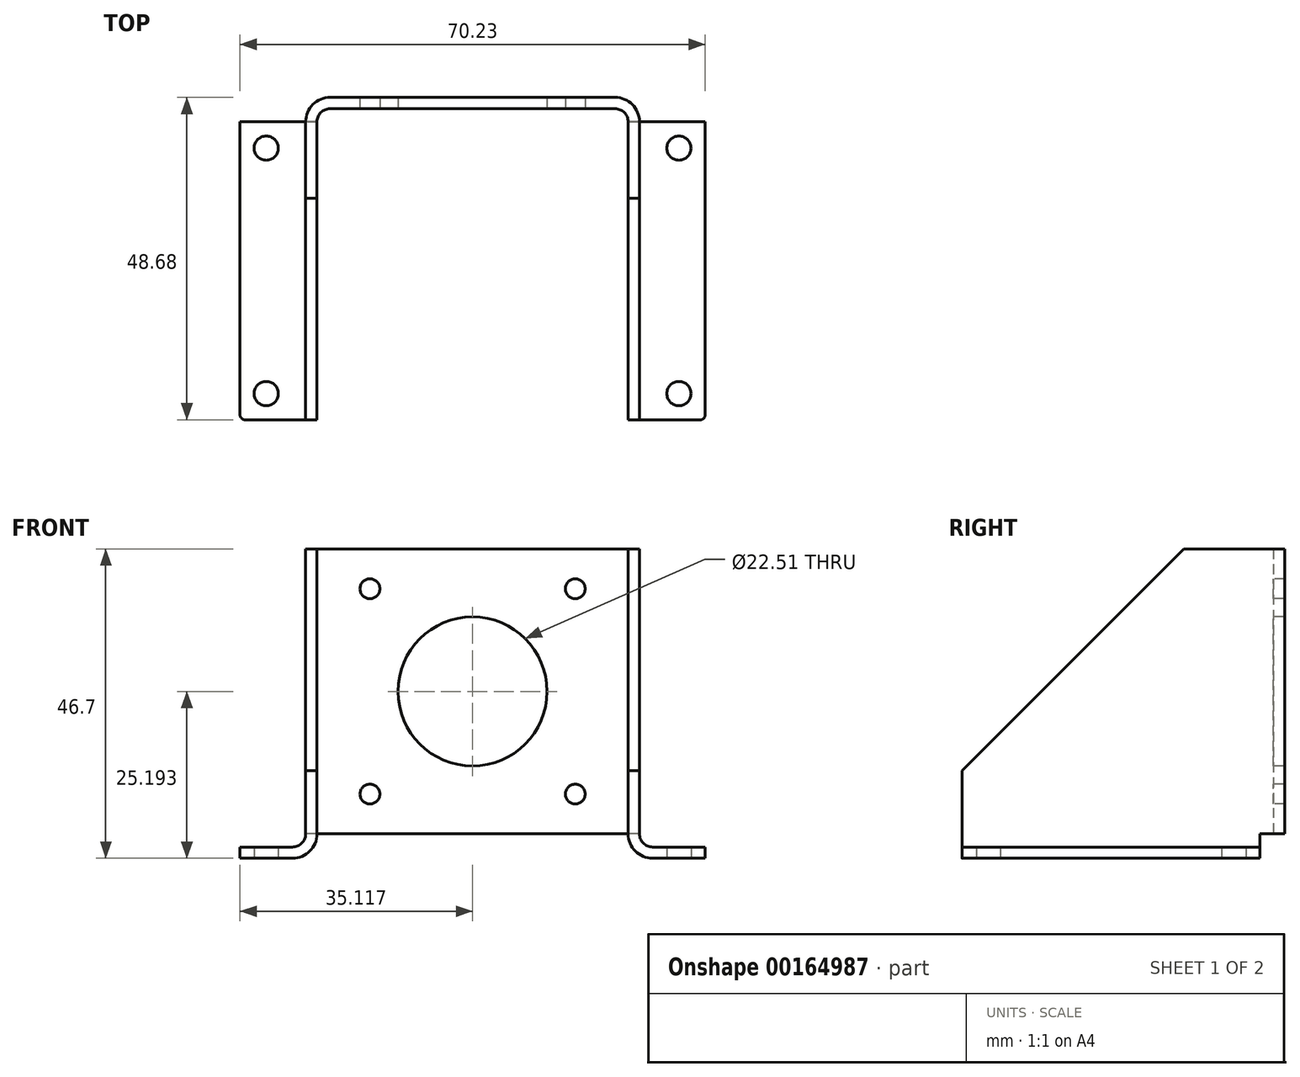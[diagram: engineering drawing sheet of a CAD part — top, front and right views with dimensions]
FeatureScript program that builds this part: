
annotation { "Feature Type Name" : "Feature", "Feature Type Description" : "" }
export const myFeature = defineFeature(function(context is Context, id is Id, definition is map)
    precondition{}
    {
        {
            var Q0;
            Q0=qCreatedBy(makeId("Top.planeOp"),FACE);
            var sketch = newSketch(context, id + "F0", { "sketchPlane" : qUnion([Q0])});
            skLineSegment(sketch, "E0.bottom", {"start": v(0, 0) * mm, "end": v(-1.7, 0) * mm});
            skLineSegment(sketch, "E1.left", {"start": v(0, 0) * mm, "end": v(0, 46.97) * mm});
            skLineSegment(sketch, "E1.right", {"start": v(-1.7, 0) * mm, "end": v(-1.7, 48.68) * mm});
            skLineSegment(sketch, "E2.bottom", {"start": v(0, 46.97) * mm, "end": v(46.97, 46.97) * mm});
            skLineSegment(sketch, "E2.top", {"start": v(-1.7, 48.68) * mm, "end": v(48.68, 48.68) * mm});
            skLineSegment(sketch, "E3.top", {"start": v(46.97, 0) * mm, "end": v(48.68, 0) * mm});
            skLineSegment(sketch, "E3.left", {"start": v(46.97, 46.97) * mm, "end": v(46.97, 0) * mm});
            skLineSegment(sketch, "E3.right", {"start": v(48.68, 48.68) * mm, "end": v(48.68, 0) * mm});
            skLineSegment(sketch, "E4", {"start": v(0, 46.97) * mm, "end": v(-1.7, 46.97) * mm, "construction": true});
            skLineSegment(sketch, "E5", {"start": v(0, 46.97) * mm, "end": v(0, 48.68) * mm, "construction": true});
            skLineSegment(sketch, "E6", {"start": v(46.97, 46.97) * mm, "end": v(48.68, 46.97) * mm, "construction": true});
            skLineSegment(sketch, "E7", {"start": v(46.97, 46.97) * mm, "end": v(46.97, 48.68) * mm, "construction": true});
            skSolve(sketch);
        }
        {
            var Q0;
            Q0=qSketchRegion(id+"F0",true);
            extrude(context, id + "F1", {"entities" : qUnion([Q0]), "depth" : 43 * mm});
        }
        {
            var Q0;
            Q0=makeQuery(id+"F1.opExtrude","SWEPT_FACE",FACE,{"disambiguationData":[OSD([sQuery(id+"F0.wireOp",EDGE,"E2.bottom")])]});
            cPlane(context, id + "F2", {"entities" : qUnion([Q0]), "cplaneType" : CPlaneType.OFFSET, "offset" : 1.98 * mm, "width" : 152.4 * mm, "height" : 152.4 * mm});
        }
        {
            var Q0;
            Q0=makeQuery(id+"F1.opExtrude","SWEPT_FACE",FACE,{"disambiguationData":[OSD([sQuery(id+"F0.wireOp",EDGE,"E3.top")])]});
            var sketch = newSketch(context, id + "F3", { "sketchPlane" : qUnion([Q0])});
            skLineSegment(sketch, "E8.bottom", {"start": v(46.97, 0) * mm, "end": v(48.68, 0) * mm});
            skLineSegment(sketch, "E8.left", {"start": v(46.97, 0) * mm, "end": v(46.97, -3.7) * mm});
            skLineSegment(sketch, "E8.right", {"start": v(48.68, 0) * mm, "end": v(48.68, -1.98) * mm});
            skLineSegment(sketch, "E9.bottom", {"start": v(48.68, -1.98) * mm, "end": v(58.6, -1.98) * mm});
            skLineSegment(sketch, "E9.top", {"start": v(46.97, -3.7) * mm, "end": v(58.6, -3.7) * mm});
            skLineSegment(sketch, "E9.right", {"start": v(58.6, -1.98) * mm, "end": v(58.6, -3.7) * mm});
            skLineSegment(sketch, "E10.bottom", {"start": v(-1.7, 0) * mm, "end": v(0, 0) * mm});
            skLineSegment(sketch, "E10.left", {"start": v(-1.7, 0) * mm, "end": v(-1.7, -1.98) * mm});
            skLineSegment(sketch, "E10.right", {"start": v(0, 0) * mm, "end": v(0, -3.7) * mm});
            skLineSegment(sketch, "E11.bottom", {"start": v(-1.7, -1.98) * mm, "end": v(-11.63, -1.98) * mm});
            skLineSegment(sketch, "E11.top", {"start": v(0, -3.7) * mm, "end": v(-11.63, -3.7) * mm});
            skLineSegment(sketch, "E11.right", {"start": v(-11.63, -1.98) * mm, "end": v(-11.63, -3.7) * mm});
            skSolve(sketch);
        }
        {
            var Q0;
            Q0=makeQuery(id+"F3.imprint","IMPRINT",FACE,{"disambiguationData":[TD([[makeQuery(id+"F3.imprint","IMPRINT",EDGE,{"derivedFrom":sQuery(id+"F3.wireOp",EDGE,"E8.bottom")}),-1.0]])]});
            var Q1;
            Q1=makeQuery(id+"F3.imprint","IMPRINT",FACE,{"disambiguationData":[TD([[makeQuery(id+"F3.imprint","IMPRINT",EDGE,{"derivedFrom":sQuery(id+"F3.wireOp",EDGE,"E10.bottom")}),-1.0]])]});
            var Q2;
            Q2=qCreatedBy(id+"F2.planeOp",FACE);
            extrude(context, id + "F4", {"entities" : qUnion([Q0, Q1]), "operationType" : NewBodyOperationType.ADD, "endBound" : BoundingType.UP_TO_SURFACE, "oppositeDirection" : true, "endBoundEntityFace" : qUnion([Q2]), "depth" : 25.4 * mm});
        }
        {
            var Q0;
            Q0=makeQuery(id+"F1.opExtrude","SWEPT_EDGE",EDGE,{"disambiguationData":[OSD([sQuery(id+"F0.wireOp",EDGE,"E1.left"),sQuery(id+"F0.wireOp",EDGE,"E2.bottom")])]});
            var Q1;
            Q1=makeQuery(id+"F1.opExtrude","SWEPT_EDGE",EDGE,{"disambiguationData":[OSD([sQuery(id+"F0.wireOp",EDGE,"E2.bottom"),sQuery(id+"F0.wireOp",EDGE,"E3.left")])]});
            var Q2;
            Q2=makeQuery(id+"F4.opExtrude","SWEPT_EDGE",EDGE,{"disambiguationData":[OSD([sQuery(id+"F3.wireOp",EDGE,"E10.left"),sQuery(id+"F3.wireOp",EDGE,"E11.bottom")])]});
            var Q3;
            Q3=makeQuery(id+"F4.opExtrude","SWEPT_EDGE",EDGE,{"disambiguationData":[OSD([sQuery(id+"F3.wireOp",EDGE,"E8.right"),sQuery(id+"F3.wireOp",EDGE,"E9.bottom")])]});
            fillet(context, id + "F5", {"entities" : qUnion([Q0, Q1, Q2, Q3]), "radius" : 1.98 * mm, "tangentPropagation" : true, "allowEdgeOverflow" : false});
        }
        {
            var Q0;
            Q0=makeQuery(id+"F1.opExtrude","SWEPT_EDGE",EDGE,{"disambiguationData":[OSD([sQuery(id+"F0.wireOp",EDGE,"E2.top"),sQuery(id+"F0.wireOp",EDGE,"E3.right")])]});
            var Q1;
            Q1=makeQuery(id+"F1.opExtrude","SWEPT_EDGE",EDGE,{"disambiguationData":[OSD([sQuery(id+"F0.wireOp",EDGE,"E1.right"),sQuery(id+"F0.wireOp",EDGE,"E2.top")])]});
            var Q2;
            Q2=makeQuery(id+"F4.opExtrude","SWEPT_EDGE",EDGE,{"disambiguationData":[OSD([sQuery(id+"F3.wireOp",EDGE,"E10.right"),sQuery(id+"F3.wireOp",EDGE,"E11.top")])]});
            var Q3;
            Q3=makeQuery(id+"F4.opExtrude","SWEPT_EDGE",EDGE,{"disambiguationData":[OSD([sQuery(id+"F3.wireOp",EDGE,"E8.left"),sQuery(id+"F3.wireOp",EDGE,"E9.top")])]});
            fillet(context, id + "F6", {"entities" : qUnion([Q0, Q1, Q2, Q3]), "radius" : 3.7 * mm, "tangentPropagation" : true, "allowEdgeOverflow" : false});
        }
        {
            var Q0;
            Q0=makeQuery(id+"F1.opExtrude","CAP_EDGE",EDGE,{"disambiguationData":[OSD([sQuery(id+"F0.wireOp",EDGE,"E0.bottom")])],"isStart":false});
            var Q1;
            Q1=makeQuery(id+"F1.opExtrude","CAP_EDGE",EDGE,{"disambiguationData":[OSD([sQuery(id+"F0.wireOp",EDGE,"E3.top")])],"isStart":false});
            chamfer(context, id + "F7", {"entities" : qUnion([Q0, Q1]), "width" : 33.48 * mm, "tangentPropagation" : true});
        }
        {
            var Q0;
            Q0=makeQuery(id+"F1.opExtrude","SWEPT_FACE",FACE,{"disambiguationData":[OSD([sQuery(id+"F0.wireOp",EDGE,"E2.bottom")])]});
            var sketch = newSketch(context, id + "F8", { "sketchPlane" : qUnion([Q0])});
            skLineSegment(sketch, "E12", {"start": v(23.49, 43) * mm, "end": v(23.49, 0) * mm, "construction": true});
            skLineSegment(sketch, "E13.bottom", {"start": v(38.99, 37) * mm, "end": v(7.99, 37) * mm, "construction": true});
            skLineSegment(sketch, "E13.top", {"start": v(38.99, 6) * mm, "end": v(7.99, 6) * mm, "construction": true});
            skLineSegment(sketch, "E13.left", {"start": v(38.99, 37) * mm, "end": v(38.99, 6) * mm, "construction": true});
            skLineSegment(sketch, "E13.right", {"start": v(7.99, 37) * mm, "end": v(7.99, 6) * mm, "construction": true});
            skPoint(sketch, "E13.middle", {"position": v(23.49, 21.5) * mm});
            skCircle(sketch, "E14", {"center": v(23.49, 21.5) * mm, "radius": 11.25 * mm});
            skCircle(sketch, "E15", {"center": v(38.99, 37) * mm, "radius": 1.5 * mm});
            skCircle(sketch, "E16", {"center": v(38.99, 6) * mm, "radius": 1.5 * mm});
            skCircle(sketch, "E17", {"center": v(7.99, 6) * mm, "radius": 1.5 * mm});
            skCircle(sketch, "E18", {"center": v(7.99, 37) * mm, "radius": 1.5 * mm});
            skSolve(sketch);
        }
        {
            var Q0;
            Q0=qSketchRegion(id+"F8",true);
            var Q1;
            Q1=makeQuery(id+"F1.opExtrude","SWEPT_FACE",FACE,{"disambiguationData":[OSD([sQuery(id+"F0.wireOp",EDGE,"E2.top")])]});
            extrude(context, id + "F9", {"entities" : qUnion([Q0]), "operationType" : NewBodyOperationType.REMOVE, "endBound" : BoundingType.UP_TO_SURFACE, "oppositeDirection" : true, "endBoundEntityFace" : qUnion([Q1]), "depth" : 25.4 * mm});
        }
        {
            var Q0;
            Q0=makeQuery(id+"F4.opExtrude","SWEPT_FACE",FACE,{"disambiguationData":[OSD([sQuery(id+"F3.wireOp",EDGE,"E11.top")])]});
            var sketch = newSketch(context, id + "F10", { "sketchPlane" : qUnion([Q0])});
            skLineSegment(sketch, "E19", {"start": v(-3.7, -22.5) * mm, "end": v(50.67, -22.5) * mm, "construction": true});
            skLineSegment(sketch, "E20.bottom", {"start": v(-11.63, -44.99) * mm, "end": v(-7.66, -44.99) * mm, "construction": true});
            skLineSegment(sketch, "E20.top", {"start": v(-11.63, -41.02) * mm, "end": v(-7.66, -41.02) * mm, "construction": true});
            skLineSegment(sketch, "E20.left", {"start": v(-11.63, -44.99) * mm, "end": v(-11.63, -41.02) * mm, "construction": true});
            skLineSegment(sketch, "E20.right", {"start": v(-7.66, -44.99) * mm, "end": v(-7.66, -41.02) * mm, "construction": true});
            skLineSegment(sketch, "E21.bottom", {"start": v(-7.66, -41.02) * mm, "end": v(54.64, -41.02) * mm, "construction": true});
            skLineSegment(sketch, "E21.top", {"start": v(-7.66, -3.97) * mm, "end": v(54.64, -3.97) * mm, "construction": true});
            skLineSegment(sketch, "E21.left", {"start": v(-7.66, -41.02) * mm, "end": v(-7.66, -3.97) * mm, "construction": true});
            skLineSegment(sketch, "E21.right", {"start": v(54.64, -41.02) * mm, "end": v(54.64, -3.97) * mm, "construction": true});
            skPoint(sketch, "E21.middle", {"position": v(23.49, -22.5) * mm});
            skCircle(sketch, "E22", {"center": v(54.64, -41.02) * mm, "radius": 1.83 * mm});
            skCircle(sketch, "E23", {"center": v(-7.66, -41.02) * mm, "radius": 1.83 * mm});
            skCircle(sketch, "E24", {"center": v(-7.66, -3.97) * mm, "radius": 1.83 * mm});
            skCircle(sketch, "E25", {"center": v(54.64, -3.97) * mm, "radius": 1.83 * mm});
            skSolve(sketch);
        }
        {
            var Q0;
            Q0=qSketchRegion(id+"F10",true);
            var Q1;
            Q1=makeQuery(id+"F4.opExtrude","SWEPT_FACE",FACE,{"disambiguationData":[OSD([sQuery(id+"F3.wireOp",EDGE,"E11.bottom")])]});
            extrude(context, id + "F11", {"entities" : qUnion([Q0]), "operationType" : NewBodyOperationType.REMOVE, "endBound" : BoundingType.UP_TO_SURFACE, "oppositeDirection" : true, "endBoundEntityFace" : qUnion([Q1]), "depth" : 25.4 * mm});
        }
        {
            var Q0;
            Q0=makeQuery(id+"F4.opExtrude","TWEAK_EDGE",EDGE,{"derivedFrom":[dummyQuery(id+"F2.planeOp",FACE),makeQuery(id+"F3.imprint","IMPRINT",EDGE,{"derivedFrom":sQuery(id+"F3.wireOp",EDGE,"E9.right")})]});
            var Q1;
            Q1=makeQuery(id+"F4.opExtrude","CAP_EDGE",EDGE,{"disambiguationData":[OSD([sQuery(id+"F3.wireOp",EDGE,"E9.right")])],"isStart":true});
            var Q2;
            Q2=makeQuery(id+"F4.opExtrude","CAP_EDGE",EDGE,{"disambiguationData":[OSD([sQuery(id+"F3.wireOp",EDGE,"E11.right")])],"isStart":true});
            var Q3;
            Q3=makeQuery(id+"F4.opExtrude","TWEAK_EDGE",EDGE,{"derivedFrom":[dummyQuery(id+"F2.planeOp",FACE),makeQuery(id+"F3.imprint","IMPRINT",EDGE,{"derivedFrom":sQuery(id+"F3.wireOp",EDGE,"E11.right")})]});
            fillet(context, id + "F12", {"entities" : qUnion([Q0, Q1, Q2, Q3]), "radius" : 0.76 * mm, "tangentPropagation" : true, "allowEdgeOverflow" : false});
        }
    });
